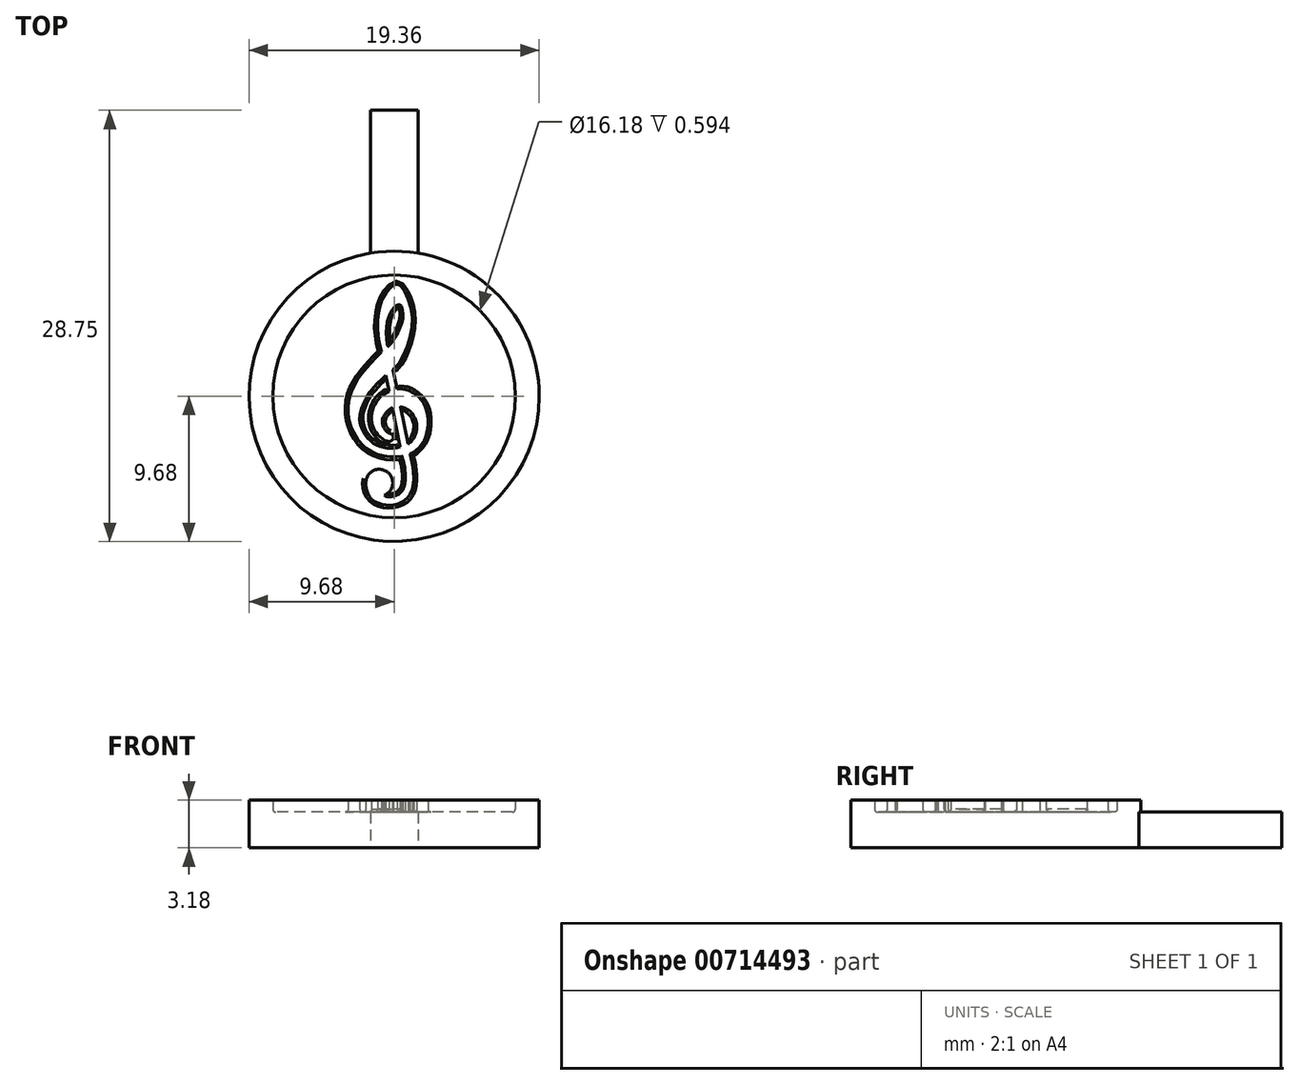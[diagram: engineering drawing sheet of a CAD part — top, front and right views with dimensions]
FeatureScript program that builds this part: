
annotation { "Feature Type Name" : "Feature", "Feature Type Description" : "" }
export const myFeature = defineFeature(function(context is Context, id is Id, definition is map)
    precondition{}
    {
        {
            var Q0;
            Q0=qCreatedBy(makeId("Top.planeOp"),FACE);
            var sketch = newSketch(context, id + "F0", { "sketchPlane" : qUnion([Q0])});
            skCircle(sketch, "E0", {"center": v(0, 0) * mm, "radius": 9.68 * mm});
            skSolve(sketch);
        }
        {
            var Q0;
            Q0=qSketchRegion(id+"F0",true);
            extrude(context, id + "F1", {"entities" : qUnion([Q0]), "depth" : 2.38 * mm, "offsetDistance" : 25.4 * mm});
        }
        {
            var Q0;
            Q0=makeQuery(id+"F1.opExtrude","CAP_FACE",FACE,{"disambiguationData":[OSD([sQuery(id+"F0.wireOp",EDGE,"E0")])],"isStart":false});
            var sketch = newSketch(context, id + "F2", { "sketchPlane" : qUnion([Q0])});
            skCircle(sketch, "E1.0.0", {"center": v(0, 0) * mm, "radius": 9.68 * mm});
            skCircle(sketch, "E2.0", {"center": v(0, 0) * mm, "radius": 8.09 * mm});
            skSolve(sketch);
        }
        {
            var Q0;
            Q0=makeQuery(id+"F2.imprint","IMPRINT",FACE,{"disambiguationData":[TD([[makeQuery(id+"F2.imprint","IMPRINT",EDGE,{"derivedFrom":sQuery(id+"F2.wireOp",EDGE,"E1.0.0")}),1.0]])]});
            extrude(context, id + "F3", {"entities" : qUnion([Q0]), "operationType" : NewBodyOperationType.ADD, "depth" : 0.8 * mm, "offsetDistance" : 25.4 * mm});
        }
        {
            var Q0;
            Q0=qCreatedBy(makeId("Top.planeOp"),FACE);
            var sketch = newSketch(context, id + "F4", { "sketchPlane" : qUnion([Q0])});
            skLineSegment(sketch, "E3.bottom", {"start": v(1.59, 9.55) * mm, "end": v(-1.59, 9.55) * mm});
            skLineSegment(sketch, "E3.top", {"start": v(1.59, 19.07) * mm, "end": v(-1.59, 19.07) * mm});
            skLineSegment(sketch, "E3.left", {"start": v(1.59, 9.55) * mm, "end": v(1.59, 19.07) * mm});
            skLineSegment(sketch, "E3.right", {"start": v(-1.59, 9.55) * mm, "end": v(-1.59, 19.07) * mm});
            skPoint(sketch, "E3.middle", {"position": v(0, 14.3) * mm});
            skSolve(sketch);
        }
        {
            var Q0;
            Q0=qSketchRegion(id+"F4",true);
            var Q1;
            Q1=makeQuery(id+"F3.opExtrude","CAP_FACE",FACE,{"disambiguationData":[OSD([sQuery(id+"F2.wireOp",EDGE,"E1.0.0"),sQuery(id+"F2.wireOp",EDGE,"E2.0")])],"isStart":false});
            extrude(context, id + "F5", {"entities" : qUnion([Q0]), "operationType" : NewBodyOperationType.ADD, "depth" : 2.38 * mm, "endBoundEntityFace" : qUnion([Q1]), "hasOffset" : true, "offsetDistance" : 1 * mm});
        }
        {
            var Q0;
            Q0=makeQuery(id+"F1.opExtrude","CAP_FACE",FACE,{"disambiguationData":[OSD([sQuery(id+"F0.wireOp",EDGE,"E0")])],"isStart":false});
            var sketch = newSketch(context, id + "F6", { "sketchPlane" : qUnion([Q0])});
            skCircle(sketch, "E4", {"center": v(-0.33, -2.73) * mm, "radius": 0.28 * mm});
            skCircle(sketch, "E5", {"center": v(-0.99, -5.77) * mm, "radius": 0.9 * mm});
            skPoint(sketch, "E6", {"position": v(0.94, -3.18) * mm});
            skPoint(sketch, "E7", {"position": v(1.07, -3.84) * mm});
            skPoint(sketch, "E8", {"position": v(0.52, -4) * mm});
            skPoint(sketch, "E9", {"position": v(0.4, -3.37) * mm});
            skPoint(sketch, "E10", {"position": v(0.42, -0.7) * mm});
            skPoint(sketch, "E11", {"position": v(0.2, 0.49) * mm});
            skPoint(sketch, "E12", {"position": v(-0.35, 0.36) * mm});
            skPoint(sketch, "E13", {"position": v(-0.11, -0.76) * mm});
            skPoint(sketch, "E14", {"position": v(-0.07, 1.77) * mm});
            skPoint(sketch, "E15", {"position": v(-0.4, 3.34) * mm});
            skPoint(sketch, "E16", {"position": v(-0.86, 2.94) * mm});
            skPoint(sketch, "E17", {"position": v(-0.55, 1.39) * mm});
            skFitSpline(sketch, "E18", {"points": [v(-0.4, 3.34) * mm, v(-0.5, 4.4) * mm, v(-0.32, 5.4) * mm, v(0.06, 5.99) * mm, v(0.37, 6.1) * mm, v(0.59, 5.58) * mm, v(0.45, 4.7) * mm, v(-0.1, 3.65) * mm, v(-0.34, 3.4) * mm, v(-0.4, 3.34) * mm]});
            skFitSpline(sketch, "E19", {"points": [v(-0.07, 1.77) * mm, v(0.72, 2.94) * mm, v(1.17, 4.47) * mm, v(1.07, 6.14) * mm, v(0.6, 7.18) * mm, v(0.39, 7.4) * mm, v(0.22, 7.48) * mm, v(-0.07, 7.37) * mm, v(-0.65, 6.74) * mm, v(-1.03, 5.6) * mm, v(-1.1, 4.85) * mm, v(-1.06, 4.02) * mm, v(-0.94, 3.34) * mm, v(-0.86, 2.94) * mm], "startDerivative": vector(10.08, 8.46) * mm, "endDerivative": vector(1.67, -5.96) * mm});
            skFitSpline(sketch, "E20", {"points": [v(-0.86, 2.94) * mm, v(-1.94, 1.79) * mm, v(-2.67, 0.7) * mm, v(-3.02, -0.29) * mm, v(-3.02, -1.45) * mm, v(-2.56, -2.67) * mm, v(-1.73, -3.55) * mm, v(-0.58, -4) * mm, v(0.52, -4) * mm], "startDerivative": vector(-8, -7.98) * mm, "endDerivative": vector(6.92, 1.32) * mm});
            skFitSpline(sketch, "E21", {"points": [v(1.07, -3.84) * mm, v(1.85, -3.2) * mm, v(2.24, -2.15) * mm, v(2.15, -0.86) * mm, v(1.57, 0.03) * mm, v(0.76, 0.45) * mm, v(0.2, 0.49) * mm], "startDerivative": vector(4.76, 2.05) * mm, "endDerivative": vector(-3.97, -0.5) * mm});
            skFitSpline(sketch, "E22", {"points": [v(-0.35, 0.36) * mm, v(-1, -0.12) * mm, v(-1.46, -1) * mm, v(-1.43, -1.94) * mm, v(-1, -2.65) * mm, v(-0.29, -3) * mm], "startDerivative": vector(-3.51, -2.1) * mm, "endDerivative": vector(3.47, 0.57) * mm});
            skFitSpline(sketch, "E23", {"points": [v(-0.27, -2.46) * mm, v(-0.66, -2.11) * mm, v(-0.77, -1.8) * mm, v(-0.73, -1.4) * mm, v(-0.11, -0.76) * mm], "startDerivative": vector(-2.41, 0.58) * mm, "endDerivative": vector(2.68, 1.3) * mm});
            skFitSpline(sketch, "E24", {"points": [v(0.42, -0.7) * mm, v(0.72, -0.8) * mm, v(1.1, -1.03) * mm, v(1.44, -1.57) * mm, v(1.5, -2.1) * mm, v(1.38, -2.68) * mm, v(1.17, -2.98) * mm, v(0.94, -3.18) * mm], "startDerivative": vector(3.65, -0.17) * mm, "endDerivative": vector(-2.5, -1.01) * mm});
            skFitSpline(sketch, "E25", {"points": [v(0.4, -3.37) * mm, v(0, -3.45) * mm, v(-0.53, -3.44) * mm, v(-1.13, -3.26) * mm, v(-1.53, -3.01) * mm, v(-2.11, -2.25) * mm, v(-2.25, -1.07) * mm, v(-1.52, 0.4) * mm, v(-0.55, 1.39) * mm], "startDerivative": vector(-4.15, -1.17) * mm, "endDerivative": vector(6.2, 5.6) * mm});
            skFitSpline(sketch, "E26", {"points": [v(0.52, -4) * mm, v(0.67, -4.6) * mm, v(0.74, -5.27) * mm, v(0.68, -6.02) * mm, v(0.22, -6.57) * mm, v(-0.4, -6.7) * mm, v(-0.66, -6.6) * mm], "startDerivative": vector(1.06, -4.4) * mm, "endDerivative": vector(-2.26, 2.1) * mm});
            skFitSpline(sketch, "E27", {"points": [v(-1.85, -5.53) * mm, v(-1.81, -6.35) * mm, v(-1.53, -6.82) * mm, v(-1.1, -7.1) * mm, v(-0.5, -7.26) * mm, v(0.14, -7.2) * mm, v(0.95, -6.71) * mm, v(1.3, -5.67) * mm, v(1.22, -4.52) * mm, v(1.07, -3.84) * mm], "startDerivative": vector(-2.02, -7.32) * mm, "endDerivative": vector(-1.17, 6.1) * mm});
            skLineSegment(sketch, "E28", {"start": v(-0.11, -0.76) * mm, "end": v(0.4, -3.37) * mm});
            skLineSegment(sketch, "E29", {"start": v(0.42, -0.7) * mm, "end": v(0.94, -3.18) * mm});
            skLineSegment(sketch, "E30", {"start": v(0.2, 0.49) * mm, "end": v(-0.07, 1.77) * mm});
            skLineSegment(sketch, "E31", {"start": v(-0.55, 1.39) * mm, "end": v(-0.35, 0.36) * mm});
            skSolve(sketch);
        }
        {
            var Q0;
            Q0 = qSketchRegion(id + "F6", true);
            var Q1;
            {var subQ0=sQuery(id+"F6.wireOp",EDGE,"E4");var subQ1=makeQuery(id+"F6.imprint","INTERSECT",VERTEX,{"derivedFrom":[subQ0,sQuery(id+"F6.wireOp",EDGE,"E22")]});Q1=makeQuery(id+"F6.imprint","IMPRINT",FACE,{"disambiguationData":[TD([[makeQuery(id+"F6.imprint","IMPRINT",EDGE,{"disambiguationData":[TD([[subQ1,1.0]])],"derivedFrom":subQ0}),1.0]])]});}
            var Q2;
            Q2=makeQuery(id+"F3.opExtrude","CAP_FACE",FACE,{"disambiguationData":[OSD([sQuery(id+"F2.wireOp",EDGE,"E1.0.0"),sQuery(id+"F2.wireOp",EDGE,"E2.0")])],"isStart":false});
            extrude(context, id + "F7", {"entities" : qUnion([Q0, Q1]), "operationType" : NewBodyOperationType.ADD, "endBound" : BoundingType.UP_TO_SURFACE, "depth" : 25 * mm, "endBoundEntityFace" : qUnion([Q2]), "offsetDistance" : 25 * mm});
        }
        {
            var Q0;
            Q0=makeQuery(id+"F1.opExtrude","CAP_FACE",FACE,{"disambiguationData":[OSD([sQuery(id+"F0.wireOp",EDGE,"E0")])],"isStart":false});
            fillet(context, id + "F8", {"entities" : qUnion([Q0]), "radius" : .2 * mm, "tangentPropagation" : true, "allowEdgeOverflow" : false});
        }
    });
